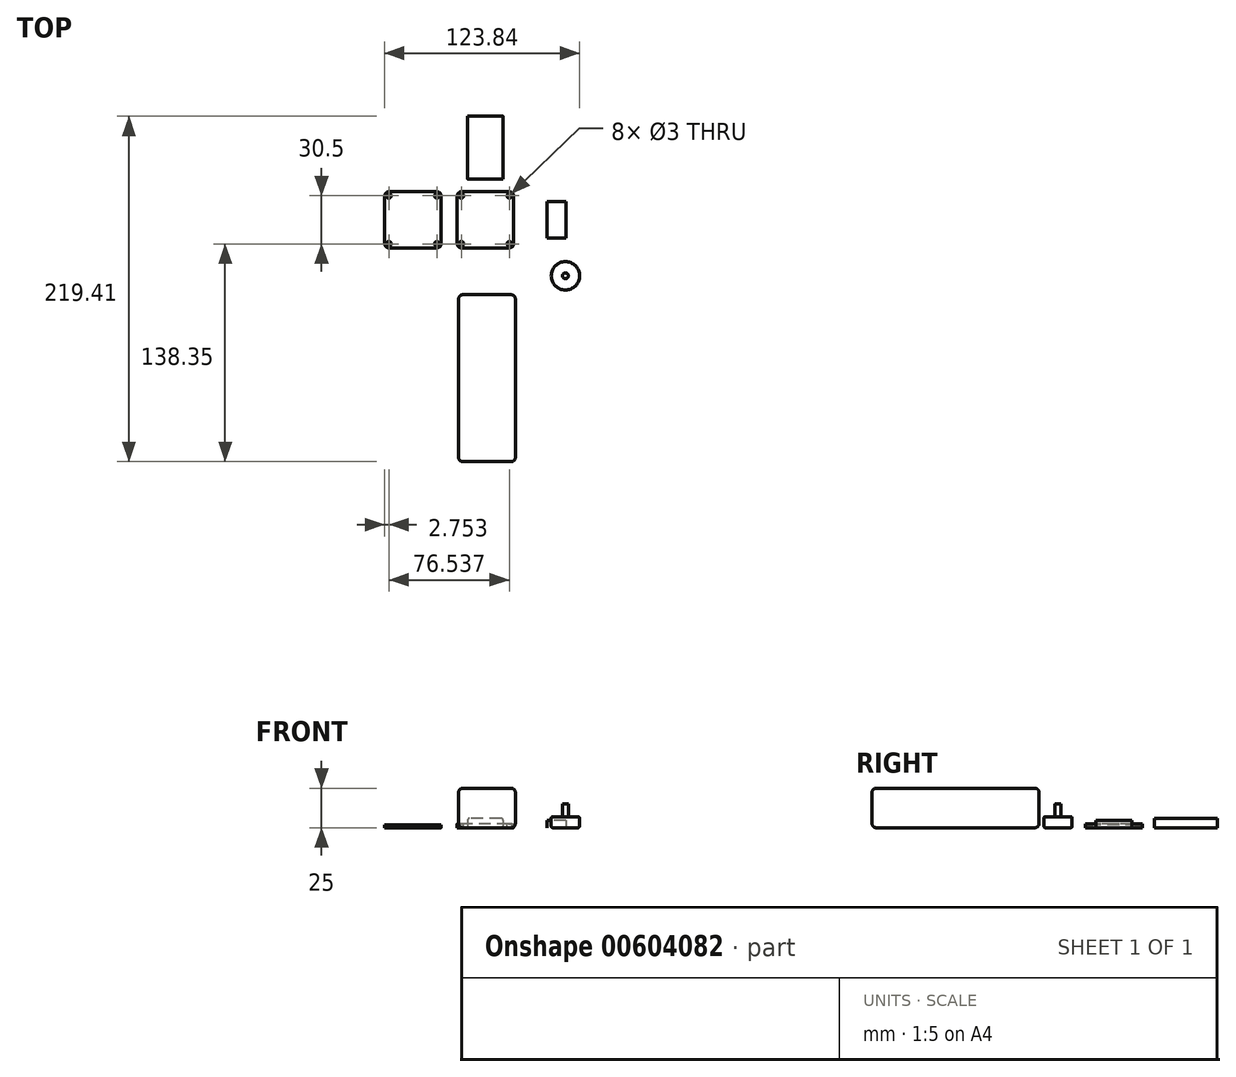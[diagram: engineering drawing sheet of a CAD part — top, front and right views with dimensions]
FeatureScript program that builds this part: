
annotation { "Feature Type Name" : "Feature", "Feature Type Description" : "" }
export const myFeature = defineFeature(function(context is Context, id is Id, definition is map)
    precondition{}
    {
        {
            var Q0;
            Q0=qCreatedBy(makeId("Top.planeOp"),FACE);
            var sketch = newSketch(context, id + "F0", { "sketchPlane" : qUnion([Q0])});
            skLineSegment(sketch, "E0.bottom", {"start": v(18, 18) * mm, "end": v(-18, 18) * mm});
            skLineSegment(sketch, "E0.top", {"start": v(18, -18) * mm, "end": v(-18, -18) * mm});
            skLineSegment(sketch, "E0.left", {"start": v(18, 18) * mm, "end": v(18, -18) * mm});
            skLineSegment(sketch, "E0.right", {"start": v(-18, 18) * mm, "end": v(-18, -18) * mm});
            skPoint(sketch, "E0.middle", {"position": v(0, 0) * mm});
            skSolve(sketch);
        }
        {
            var Q0;
            Q0 = qSketchRegion(id + "F0", true);
            extrude(context, id + "F1", {"entities" : qUnion([Q0]), "depth" : 2.54 * mm, "offsetDistance" : 25.4 * mm});
        }
        {
            var Q0;
            Q0=makeQuery(id+"F1.opExtrude","SWEPT_EDGE",EDGE,{"disambiguationData":[OSD([sQuery(id+"F0.wireOp",EDGE,"E0.bottom"),sQuery(id+"F0.wireOp",EDGE,"E0.right")])]});
            var Q1;
            Q1=makeQuery(id+"F1.opExtrude","SWEPT_EDGE",EDGE,{"disambiguationData":[OSD([sQuery(id+"F0.wireOp",EDGE,"E0.bottom"),sQuery(id+"F0.wireOp",EDGE,"E0.left")])]});
            var Q2;
            Q2=makeQuery(id+"F1.opExtrude","SWEPT_EDGE",EDGE,{"disambiguationData":[OSD([sQuery(id+"F0.wireOp",EDGE,"E0.top"),sQuery(id+"F0.wireOp",EDGE,"E0.left")])]});
            var Q3;
            Q3=makeQuery(id+"F1.opExtrude","SWEPT_EDGE",EDGE,{"disambiguationData":[OSD([sQuery(id+"F0.wireOp",EDGE,"E0.top"),sQuery(id+"F0.wireOp",EDGE,"E0.right")])]});
            fillet(context, id + "F2", {"entities" : qUnion([Q0, Q1, Q2, Q3]), "radius" : 3.17 * mm, "tangentPropagation" : true, "allowEdgeOverflow" : false});
        }
        {
            var Q0;
            Q0=makeQuery(id+"F1.opExtrude","CAP_FACE",FACE,{"disambiguationData":[OSD([sQuery(id+"F0.wireOp",EDGE,"E0.bottom"),sQuery(id+"F0.wireOp",EDGE,"E0.top"),sQuery(id+"F0.wireOp",EDGE,"E0.left"),sQuery(id+"F0.wireOp",EDGE,"E0.right")])],"isStart":false});
            var sketch = newSketch(context, id + "F3", { "sketchPlane" : qUnion([Q0])});
            skLineSegment(sketch, "E1.bottom", {"start": v(15.25, 15.25) * mm, "end": v(-15.25, 15.25) * mm, "construction": true});
            skLineSegment(sketch, "E1.top", {"start": v(15.25, -15.25) * mm, "end": v(-15.25, -15.25) * mm, "construction": true});
            skLineSegment(sketch, "E1.left", {"start": v(15.25, 15.25) * mm, "end": v(15.25, -15.25) * mm, "construction": true});
            skLineSegment(sketch, "E1.right", {"start": v(-15.25, 15.25) * mm, "end": v(-15.25, -15.25) * mm, "construction": true});
            skPoint(sketch, "E1.middle", {"position": v(0, 0) * mm});
            skCircle(sketch, "E2", {"center": v(-15.25, 15.25) * mm, "radius": 1.5 * mm});
            skLineSegment(sketch, "E3", {"start": v(-18, 0) * mm, "end": v(18, 0) * mm, "construction": true});
            skLineSegment(sketch, "E4", {"start": v(0, 18) * mm, "end": v(0, -18) * mm, "construction": true});
            skCircle(sketch, "E5.MirrorC", {"center": v(15.25, 15.25) * mm, "radius": 1.5 * mm});
            skCircle(sketch, "E6.MirrorC", {"center": v(-15.25, -15.25) * mm, "radius": 1.5 * mm});
            skCircle(sketch, "E7.MirrorC", {"center": v(15.25, -15.25) * mm, "radius": 1.5 * mm});
            skSolve(sketch);
        }
        {
            var Q0;
            Q0 = qSketchRegion(id + "F3", true);
            extrude(context, id + "F4", {"entities" : qUnion([Q0]), "operationType" : NewBodyOperationType.REMOVE, "oppositeDirection" : true, "depth" : 2.54 * mm, "offsetDistance" : 25.4 * mm});
        }
        {
            var Q0;
            Q0=qCreatedBy(makeId("Top.planeOp"),FACE);
            var sketch = newSketch(context, id + "F5", { "sketchPlane" : qUnion([Q0])});
            skLineSegment(sketch, "E8.bottom", {"start": v(51.23, 11.5) * mm, "end": v(39.23, 11.5) * mm});
            skLineSegment(sketch, "E8.top", {"start": v(51.23, -11.5) * mm, "end": v(39.23, -11.5) * mm});
            skLineSegment(sketch, "E8.left", {"start": v(51.23, 11.5) * mm, "end": v(51.23, -11.5) * mm});
            skLineSegment(sketch, "E8.right", {"start": v(39.23, 11.5) * mm, "end": v(39.23, -11.5) * mm});
            skPoint(sketch, "E8.middle", {"position": v(45.23, 0) * mm});
            skSolve(sketch);
        }
        {
            var Q0;
            Q0 = qSketchRegion(id + "F5", true);
            extrude(context, id + "F6", {"entities" : qUnion([Q0]), "depth" : 4.5 * mm, "offsetDistance" : 25.4 * mm});
        }
        {
            var Q0;
            Q0=qCreatedBy(makeId("Top.planeOp"),FACE);
            var sketch = newSketch(context, id + "F7", { "sketchPlane" : qUnion([Q0])});
            skLineSegment(sketch, "E9.bottom", {"start": v(-28.04, 18) * mm, "end": v(-64.04, 18) * mm});
            skLineSegment(sketch, "E9.top", {"start": v(-28.04, -18) * mm, "end": v(-64.04, -18) * mm});
            skLineSegment(sketch, "E9.left", {"start": v(-28.04, 18) * mm, "end": v(-28.04, -18) * mm});
            skLineSegment(sketch, "E9.right", {"start": v(-64.04, 18) * mm, "end": v(-64.04, -18) * mm});
            skPoint(sketch, "E9.middle", {"position": v(-46.04, 0) * mm});
            skSolve(sketch);
        }
        {
            var Q0;
            Q0 = qSketchRegion(id + "F7", true);
            extrude(context, id + "F8", {"entities" : qUnion([Q0]), "depth" : 1.75 * mm, "offsetDistance" : 25.4 * mm});
        }
        {
            var Q0;
            Q0=makeQuery(id+"F8.opExtrude","CAP_FACE",FACE,{"disambiguationData":[OSD([sQuery(id+"F7.wireOp",EDGE,"E9.bottom"),sQuery(id+"F7.wireOp",EDGE,"E9.top"),sQuery(id+"F7.wireOp",EDGE,"E9.left"),sQuery(id+"F7.wireOp",EDGE,"E9.right")])],"isStart":false});
            var sketch = newSketch(context, id + "F9", { "sketchPlane" : qUnion([Q0])});
            skLineSegment(sketch, "E10", {"start": v(-46.04, 18) * mm, "end": v(-46.04, -18) * mm, "construction": true});
            skLineSegment(sketch, "E11", {"start": v(-64.04, 0) * mm, "end": v(-28.04, 0) * mm, "construction": true});
            skLineSegment(sketch, "E12.bottom", {"start": v(-30.79, 15.25) * mm, "end": v(-61.29, 15.25) * mm, "construction": true});
            skLineSegment(sketch, "E12.top", {"start": v(-30.79, -15.25) * mm, "end": v(-61.29, -15.25) * mm, "construction": true});
            skLineSegment(sketch, "E12.left", {"start": v(-30.79, 15.25) * mm, "end": v(-30.79, -15.25) * mm, "construction": true});
            skLineSegment(sketch, "E12.right", {"start": v(-61.29, 15.25) * mm, "end": v(-61.29, -15.25) * mm, "construction": true});
            skPoint(sketch, "E12.middle", {"position": v(-46.04, 0) * mm});
            skCircle(sketch, "E13", {"center": v(-61.29, 15.25) * mm, "radius": 1.5 * mm});
            skCircle(sketch, "E14.MirrorC", {"center": v(-30.79, 15.25) * mm, "radius": 1.5 * mm});
            skCircle(sketch, "E15.MirrorC", {"center": v(-61.29, -15.25) * mm, "radius": 1.5 * mm});
            skCircle(sketch, "E16.MirrorC", {"center": v(-30.79, -15.25) * mm, "radius": 1.5 * mm});
            skSolve(sketch);
        }
        {
            var Q0;
            Q0 = qSketchRegion(id + "F9", true);
            extrude(context, id + "F10", {"entities" : qUnion([Q0]), "operationType" : NewBodyOperationType.REMOVE, "oppositeDirection" : true, "depth" : 1.75 * mm, "offsetDistance" : 25.4 * mm});
        }
        {
            var Q0;
            Q0=makeQuery(id+"F8.opExtrude","SWEPT_EDGE",EDGE,{"disambiguationData":[OSD([sQuery(id+"F7.wireOp",EDGE,"E9.bottom"),sQuery(id+"F7.wireOp",EDGE,"E9.right")])]});
            var Q1;
            Q1=makeQuery(id+"F8.opExtrude","SWEPT_EDGE",EDGE,{"disambiguationData":[OSD([sQuery(id+"F7.wireOp",EDGE,"E9.bottom"),sQuery(id+"F7.wireOp",EDGE,"E9.left")])]});
            var Q2;
            Q2=makeQuery(id+"F8.opExtrude","SWEPT_EDGE",EDGE,{"disambiguationData":[OSD([sQuery(id+"F7.wireOp",EDGE,"E9.top"),sQuery(id+"F7.wireOp",EDGE,"E9.left")])]});
            var Q3;
            Q3=makeQuery(id+"F8.opExtrude","SWEPT_EDGE",EDGE,{"disambiguationData":[OSD([sQuery(id+"F7.wireOp",EDGE,"E9.top"),sQuery(id+"F7.wireOp",EDGE,"E9.right")])]});
            fillet(context, id + "F11", {"entities" : qUnion([Q0, Q1, Q2, Q3]), "radius" : 3.17 * mm, "tangentPropagation" : true, "allowEdgeOverflow" : false});
        }
        {
            var Q0;
            Q0=qCreatedBy(makeId("Top.planeOp"),FACE);
            var sketch = newSketch(context, id + "F12", { "sketchPlane" : qUnion([Q0])});
            skLineSegment(sketch, "E17.bottom", {"start": v(11.25, 65.81) * mm, "end": v(11.25, 25.81) * mm});
            skLineSegment(sketch, "E17.top", {"start": v(-11.25, 65.81) * mm, "end": v(-11.25, 25.81) * mm});
            skLineSegment(sketch, "E17.left", {"start": v(11.25, 65.81) * mm, "end": v(-11.25, 65.81) * mm});
            skLineSegment(sketch, "E17.right", {"start": v(11.25, 25.81) * mm, "end": v(-11.25, 25.81) * mm});
            skPoint(sketch, "E17.middle", {"position": v(0, 45.81) * mm});
            skSolve(sketch);
        }
        {
            var Q0;
            Q0 = qSketchRegion(id + "F12", true);
            extrude(context, id + "F13", {"entities" : qUnion([Q0]), "depth" : 6 * mm, "offsetDistance" : 25.4 * mm});
        }
        {
            var Q0;
            Q0=makeQuery(id+"F13.opExtrude","CAP_EDGE",EDGE,{"disambiguationData":[OSD([sQuery(id+"F12.wireOp",EDGE,"E17.bottom")])],"isStart":false});
            var Q1;
            Q1=makeQuery(id+"F13.opExtrude","CAP_EDGE",EDGE,{"disambiguationData":[OSD([sQuery(id+"F12.wireOp",EDGE,"E17.bottom")])],"isStart":true});
            var Q2;
            Q2=makeQuery(id+"F13.opExtrude","CAP_EDGE",EDGE,{"disambiguationData":[OSD([sQuery(id+"F12.wireOp",EDGE,"E17.top")])],"isStart":true});
            var Q3;
            Q3=makeQuery(id+"F13.opExtrude","CAP_EDGE",EDGE,{"disambiguationData":[OSD([sQuery(id+"F12.wireOp",EDGE,"E17.top")])],"isStart":false});
            fillet(context, id + "F14", {"entities" : qUnion([Q0, Q1, Q2, Q3]), "radius" : 1.27 * mm, "tangentPropagation" : true, "allowEdgeOverflow" : false});
        }
        {
            var Q0;
            Q0=qCreatedBy(makeId("Top.planeOp"),FACE);
            var sketch = newSketch(context, id + "F15", { "sketchPlane" : qUnion([Q0])});
            skLineSegment(sketch, "E18.bottom", {"start": v(-17, -47.6) * mm, "end": v(-17, -153.6) * mm});
            skLineSegment(sketch, "E18.top", {"start": v(19, -47.6) * mm, "end": v(19, -153.6) * mm});
            skLineSegment(sketch, "E18.left", {"start": v(-17, -47.6) * mm, "end": v(19, -47.6) * mm});
            skLineSegment(sketch, "E18.right", {"start": v(-17, -153.6) * mm, "end": v(19, -153.6) * mm});
            skPoint(sketch, "E18.middle", {"position": v(1, -100.6) * mm});
            skLineSegment(sketch, "E19", {"start": v(0, 0) * mm, "end": v(0, -101.6) * mm, "construction": true});
            skSolve(sketch);
        }
        {
            var Q0;
            Q0 = qSketchRegion(id + "F15", true);
            extrude(context, id + "F16", {"entities" : qUnion([Q0]), "depth" : 25 * mm, "offsetDistance" : 25.4 * mm});
        }
        {
            var Q0;
            Q0=makeQuery(id+"F16.opExtrude","CAP_FACE",FACE,{"disambiguationData":[OSD([sQuery(id+"F15.wireOp",EDGE,"E18.bottom"),sQuery(id+"F15.wireOp",EDGE,"E18.top"),sQuery(id+"F15.wireOp",EDGE,"E18.left"),sQuery(id+"F15.wireOp",EDGE,"E18.right")])],"isStart":false});
            var Q1;
            Q1=makeQuery(id+"F16.opExtrude","SWEPT_FACE",FACE,{"disambiguationData":[OSD([sQuery(id+"F15.wireOp",EDGE,"E18.right")])]});
            var Q2;
            Q2=makeQuery(id+"F16.opExtrude","CAP_FACE",FACE,{"disambiguationData":[OSD([sQuery(id+"F15.wireOp",EDGE,"E18.bottom"),sQuery(id+"F15.wireOp",EDGE,"E18.top"),sQuery(id+"F15.wireOp",EDGE,"E18.left"),sQuery(id+"F15.wireOp",EDGE,"E18.right")])],"isStart":true});
            var Q3;
            Q3=makeQuery(id+"F16.opExtrude","SWEPT_FACE",FACE,{"disambiguationData":[OSD([sQuery(id+"F15.wireOp",EDGE,"E18.left")])]});
            fillet(context, id + "F17", {"entities" : qUnion([Q0, Q1, Q2, Q3]), "radius" : 2.54 * mm, "tangentPropagation" : true, "allowEdgeOverflow" : false});
        }
        {
            var Q0;
            Q0=qCreatedBy(makeId("Top.planeOp"),FACE);
            var sketch = newSketch(context, id + "F18", { "sketchPlane" : qUnion([Q0])});
            skLineSegment(sketch, "E20", {"start": v(0, 0) * mm, "end": v(0, -35.56) * mm, "construction": true});
            skLineSegment(sketch, "E21", {"start": v(0, -35.56) * mm, "end": v(50.8, -35.56) * mm, "construction": true});
            skCircle(sketch, "E22", {"center": v(50.8, -35.56) * mm, "radius": 9 * mm});
            skSolve(sketch);
        }
        {
            var Q0;
            Q0 = qSketchRegion(id + "F18", true);
            extrude(context, id + "F19", {"entities" : qUnion([Q0]), "depth" : 7 * mm, "offsetDistance" : 25.4 * mm});
        }
        {
            var Q0;
            Q0=makeQuery(id+"F19.opExtrude","CAP_FACE",FACE,{"disambiguationData":[OSD([sQuery(id+"F18.wireOp",EDGE,"E22")])],"isStart":false});
            var sketch = newSketch(context, id + "F20", { "sketchPlane" : qUnion([Q0])});
            skCircle(sketch, "E23", {"center": v(50.8, -35.56) * mm, "radius": 1.84 * mm});
            skSolve(sketch);
        }
        {
            var Q0;
            Q0 = qSketchRegion(id + "F20", true);
            extrude(context, id + "F21", {"entities" : qUnion([Q0]), "operationType" : NewBodyOperationType.ADD, "depth" : 8 * mm, "offsetDistance" : 25.4 * mm});
        }
        {
            var Q0;
            Q0=makeQuery(id+"F19.opExtrude","CAP_FACE",FACE,{"disambiguationData":[OSD([sQuery(id+"F18.wireOp",EDGE,"E22")])],"isStart":true});
            var Q1;
            Q1=makeQuery(id+"F19.opExtrude","CAP_FACE",FACE,{"disambiguationData":[OSD([sQuery(id+"F18.wireOp",EDGE,"E22")])],"isStart":false});
            fillet(context, id + "F22", {"entities" : qUnion([Q0, Q1]), "radius" : 1 * mm, "tangentPropagation" : true, "allowEdgeOverflow" : false});
        }
    });
